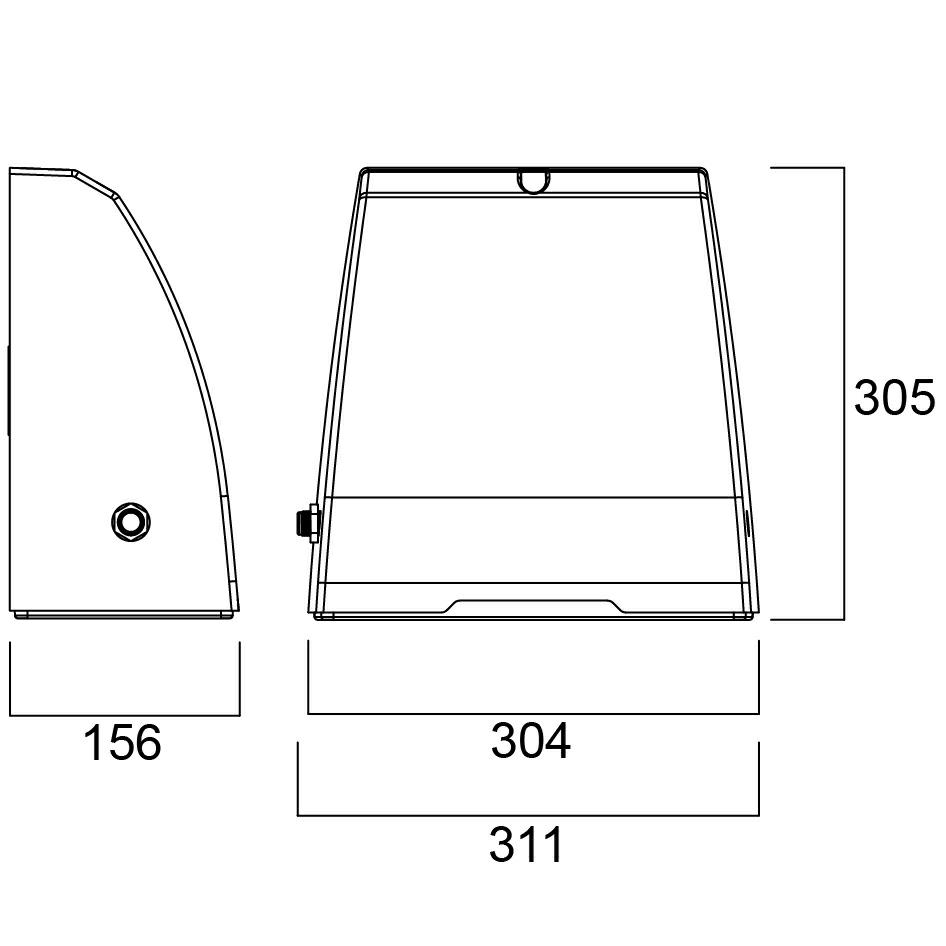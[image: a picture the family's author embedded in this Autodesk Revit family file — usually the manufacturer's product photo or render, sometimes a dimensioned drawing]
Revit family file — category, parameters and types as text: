
# Revit family: 0049944_1900lm
name_source: partatom
category: Lighting Fixtures
revit_build: Autodesk Revit 2018 (Build: 20170223_1515(x64)
units: mm (PartAtom-declared; Revit-internal decimal feet)

## family parameters
Cut with Voids When Loaded = No
Host = Face
Light Source = Yes
OmniClass Number = 23.80.70.00
OmniClass Title = Lighting
Part Type = Normal
Room Calculation Point = No
Round Connector Dimension = Use Diameter
Shared = No

## types (1)
- 0049944 MURO SURF IP65 1700-3250LM 840 PH GR
    Apparent Load = 28 VA
    Assembly Code = D5020200
    AssetType = Fixed
    ClassificationName = Uniclass2015
    ClassificationValue = EF_70_80
    Color Filter = 16777215
    Cost = 0 $
    Default Elevation = 1219 mm
    Description = Muro Surface is a wall mounted fixture for exterior lighting applications. Comes with aluminium housing in RAL7016 anthracite grey colour, frosted PC diffuser, IP65, IK10, Class I, 4000K, non-dimmable multipower driver with 5 settings, 1700 / 1900 / 2750 / 3150 / 3250 lm, 14 / 16 / 24 / 27 / 28 W, up to 121 lm/W total system efficacy, switchable built in Mini photocell, CRI80, Asymmetrical beam, 119.000 hrs L70B50 lifespan, 304 x 305 x 155 mm (L x W x D) dimensions, 4.1 kg weight.
    Dimming Lamp Color Temperature Shift = <None>
    DocumentationLiterature = http://www.sylvania-lighting.com
    ElectricShockClassification = 116
    Emit Shape Visible in Rendering = No
    Emit from Circle Diameter = 610 mm
    IfcExportAs = Class I
    IfcExportType = IfcLightFixtureType
    ImpactProtectionIndex = IfcLightFixtureType
    IngressProtection = IfcLightFixtureType
    InputNominalFrequency = 4000
    InputVoltage = 0
    LampColourRenderingIndex = 16500
    LampColourTemperature = LED
    LampMacAdamStep = 80
    LampNominalLuminous = 4000 K
    LightOutputRatio = LED
    LuminaireType = 0
    ManufacturerName = 116 lm/W
    Material = Feilo Sylvania
    Material_1_SYL = <By Category>
    Material_2_SYL = <By Category>
    Material_3_SYL = <By Category>
    Material_4_SYL = <By Category>
    Model = Muro Surface IP65 1700-3250lm 840 PH Grey
    ModelNumber = 0049944
    ModelReference = Muro Surface IP65 1700-3250lm 840 PH Grey
    Name = Muro Surface IP65 1700-3250lm 840 PH Grey
    NominalDepth = 155 mm  [stored 0.50853 ft]
    NominalHeight = 305 mm  [stored 1.00066 ft]
    NominalLength = 155 mm  [stored 0.50853 ft]
    Photometric Web File = 0049944_1900lm.IES
    PowerConsumption = Lighting
    PowerFactor = 0.95
    Tilt Angle = -90.00°
    Type Image = <None>
    TypeName = Muro Surface IP65 1700-3250lm 840 PH Grey
    URL = 0.9
    Voltage = 0 V
    WarrantyDescription = http://www.sylvania-lighting.com

note: [stored X ft] marks values corroborated as IEEE doubles in the binary element streams (Revit-internal decimal feet)

## geometry (parser evidence)
native form markers: Sweep x1
no freeform markers — native parametric forms only
